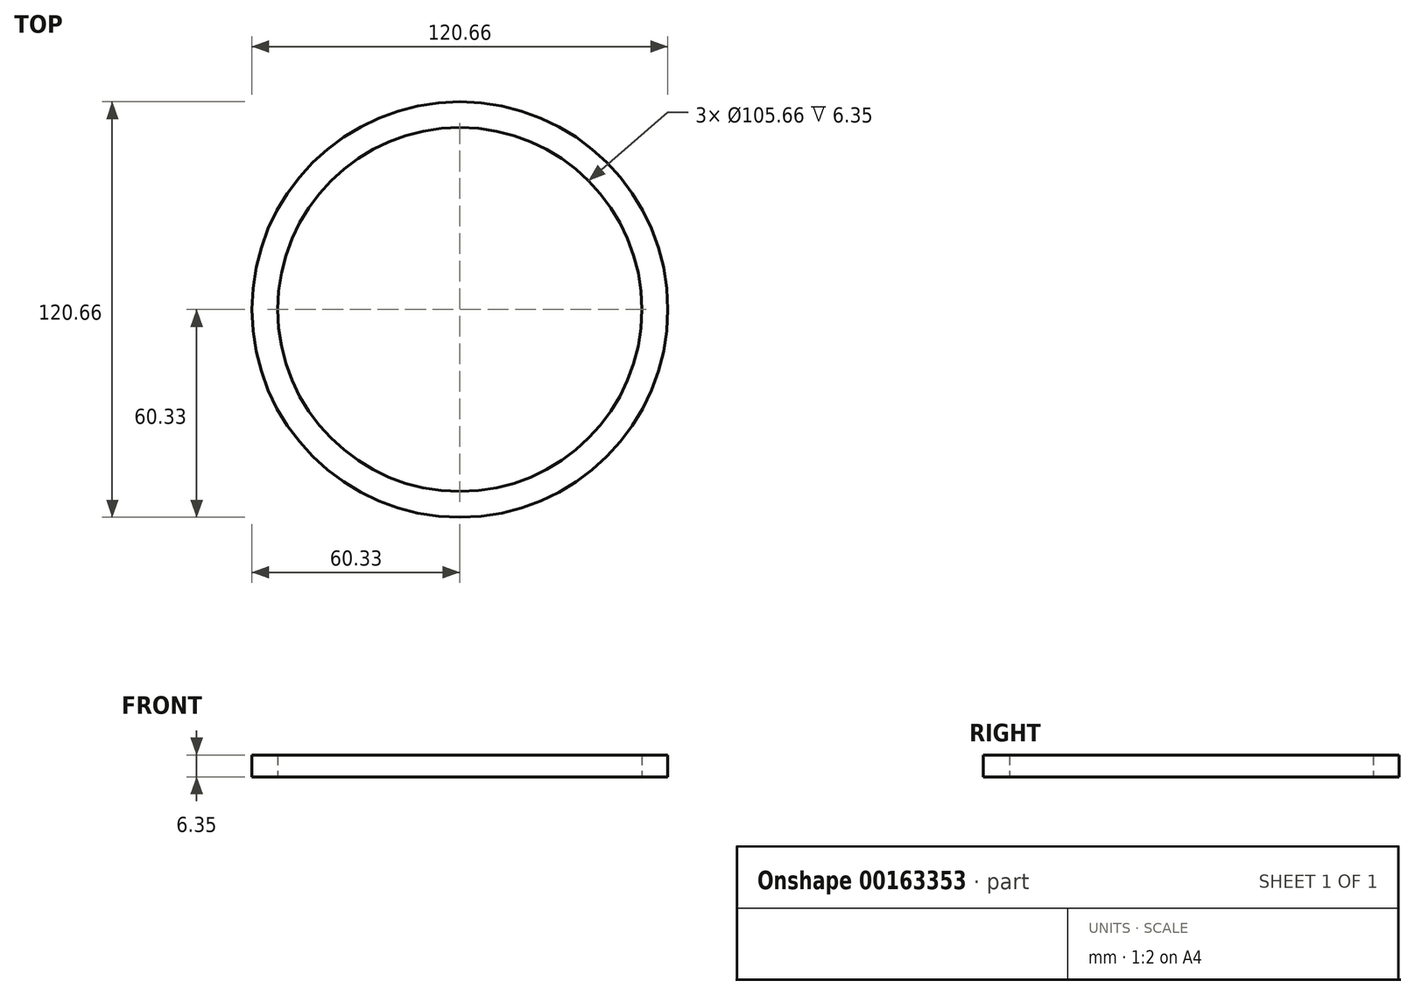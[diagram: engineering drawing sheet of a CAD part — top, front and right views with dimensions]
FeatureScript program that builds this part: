
annotation { "Feature Type Name" : "Feature", "Feature Type Description" : "" }
export const myFeature = defineFeature(function(context is Context, id is Id, definition is map)
    precondition{}
    {
        {
            var Q0;
            Q0=qCreatedBy(makeId("Top.planeOp"),FACE);
            var sketch = newSketch(context, id + "F0", { "sketchPlane" : qUnion([Q0])});
            skCircle(sketch, "E0", {"center": v(0, 0) * mm, "radius": 52.83 * mm});
            skCircle(sketch, "E1", {"center": v(0, 0) * mm, "radius": 60.33 * mm});
            skSolve(sketch);
        }
        {
            var Q0;
            Q0=makeQuery(id+"F0.imprint","IMPRINT",FACE,{"disambiguationData":[TD([[makeQuery(id+"F0.imprint","IMPRINT",EDGE,{"derivedFrom":sQuery(id+"F0.wireOp",EDGE,"E0")}),-1.0]])]});
            extrude(context, id + "F1", {"entities" : qUnion([Q0]), "depth" : 6.35 * mm});
        }
    });
